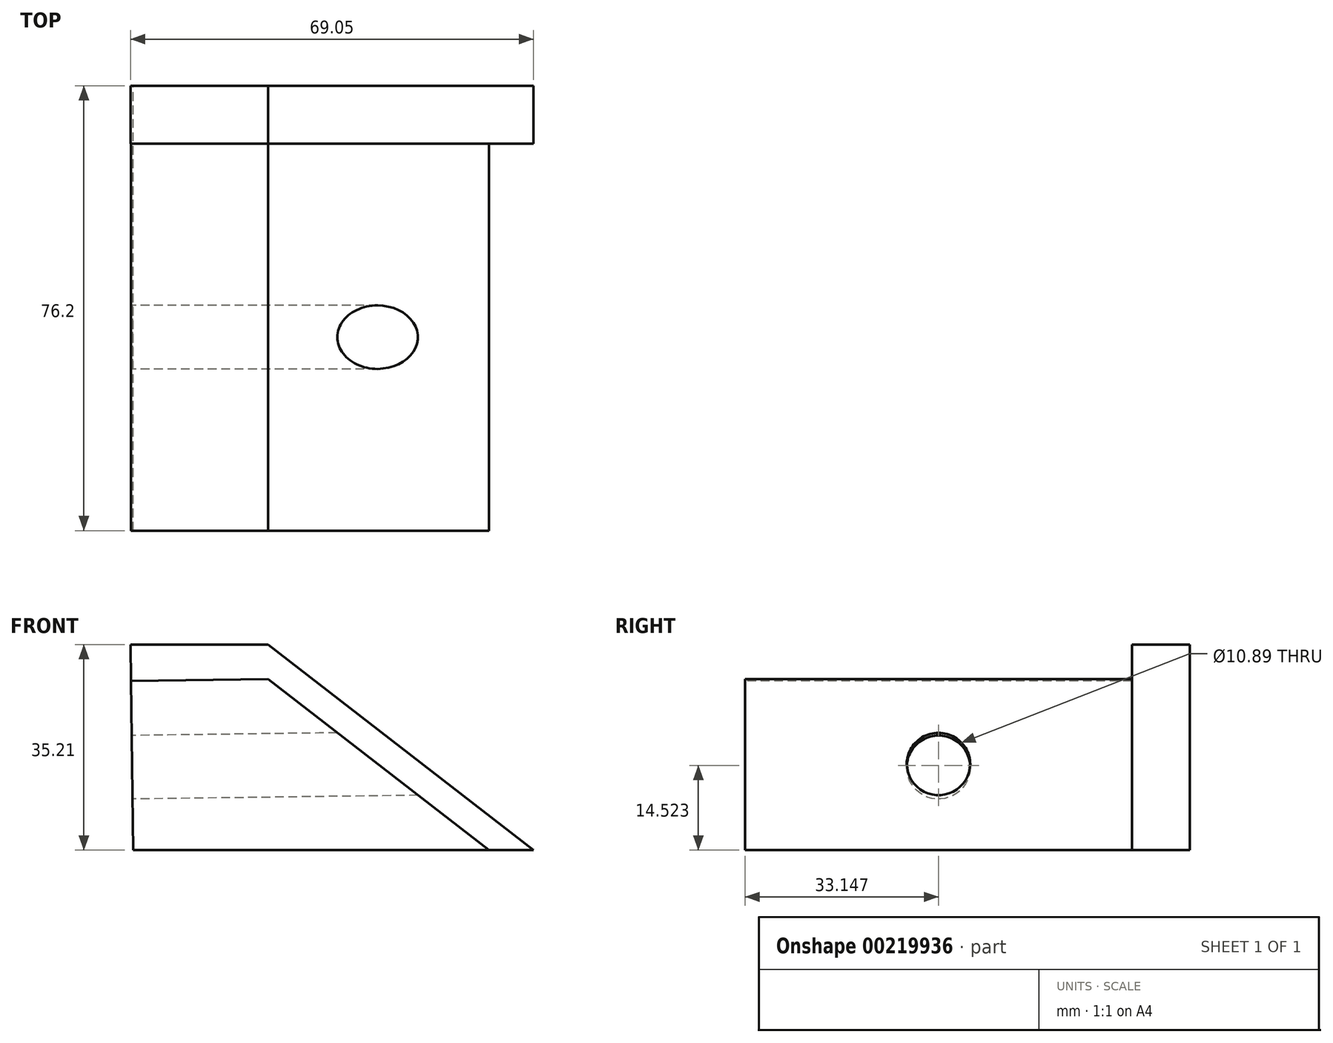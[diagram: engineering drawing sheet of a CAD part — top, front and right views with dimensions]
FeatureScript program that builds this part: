
annotation { "Feature Type Name" : "Feature", "Feature Type Description" : "" }
export const myFeature = defineFeature(function(context is Context, id is Id, definition is map)
    precondition{}
    {
        {
            var Q0;
            Q0=qCreatedBy(makeId("Front.planeOp"),FACE);
            var sketch = newSketch(context, id + "F0", { "sketchPlane" : qUnion([Q0])});
            skLineSegment(sketch, "E0", {"start": v(-34.17, 0) * mm, "end": v(34.4, 0) * mm});
            skLineSegment(sketch, "E1", {"start": v(34.4, 0) * mm, "end": v(-11.08, 35.21) * mm});
            skLineSegment(sketch, "E2", {"start": v(-11.08, 35.21) * mm, "end": v(-34.64, 35.21) * mm});
            skLineSegment(sketch, "E3", {"start": v(-34.64, 35.21) * mm, "end": v(-34.17, 0) * mm});
            skSolve(sketch);
        }
        {
            var Q0;
            Q0 = qSketchRegion(id + "F0", true);
            extrude(context, id + "F1", {"entities" : qUnion([Q0]), "depth" : 76.2 * mm});
        }
        {
            var Q0;
            Q0=makeQuery(id+"F1.opExtrude","CAP_FACE",FACE,{"disambiguationData":[OSD([sQuery(id+"F0.wireOp",EDGE,"E0"),sQuery(id+"F0.wireOp",EDGE,"E1"),sQuery(id+"F0.wireOp",EDGE,"E2"),sQuery(id+"F0.wireOp",EDGE,"E3")])],"isStart":false});
            var sketch = newSketch(context, id + "F2", { "sketchPlane" : qUnion([Q0])});
            skLineSegment(sketch, "E4", {"start": v(26.75, 0) * mm, "end": v(34.4, 0) * mm});
            skLineSegment(sketch, "E5", {"start": v(34.4, 0) * mm, "end": v(-11.08, 35.21) * mm});
            skLineSegment(sketch, "E6", {"start": v(-11.08, 35.21) * mm, "end": v(-34.64, 35.21) * mm});
            skLineSegment(sketch, "E7", {"start": v(-34.64, 35.21) * mm, "end": v(-34.55, 28.98) * mm});
            skLineSegment(sketch, "E8", {"start": v(-34.55, 28.98) * mm, "end": v(-11.08, 29.3) * mm});
            skLineSegment(sketch, "E9", {"start": v(-11.08, 29.3) * mm, "end": v(26.75, 0) * mm});
            skSolve(sketch);
        }
        {
            var Q0;
            Q0 = qSketchRegion(id + "F2", true);
            extrude(context, id + "F3", {"entities" : qUnion([Q0]), "operationType" : NewBodyOperationType.REMOVE, "oppositeDirection" : true, "depth" : 66.3 * mm});
        }
        {
            var Q0;
            Q0=makeQuery(id+"F1.opExtrude","SWEPT_FACE",FACE,{"disambiguationData":[OSD([sQuery(id+"F0.wireOp",EDGE,"E3")])]});
            var sketch = newSketch(context, id + "F4", { "sketchPlane" : qUnion([Q0])});
            skLineSegment(sketch, "E10.bottom", {"start": v(9.9, 29.43) * mm, "end": v(76.2, 29.43) * mm});
            skLineSegment(sketch, "E10.top", {"start": v(9.9, 0.45) * mm, "end": v(76.2, 0.45) * mm});
            skLineSegment(sketch, "E10.left", {"start": v(9.9, 29.43) * mm, "end": v(9.9, 0.45) * mm});
            skLineSegment(sketch, "E10.right", {"start": v(76.2, 29.43) * mm, "end": v(76.2, 0.45) * mm});
            skCircle(sketch, "E11", {"center": v(43.05, 14.65) * mm, "radius": 5.44 * mm});
            skPoint(sketch, "E11.centerSnap0", {"position": v(43.05, 0.45) * mm});
            skSolve(sketch);
        }
        {
            var Q0;
            Q0=makeQuery(id+"F4.imprint","IMPRINT",FACE,{"disambiguationData":[TD([[makeQuery(id+"F4.imprint","IMPRINT",EDGE,{"derivedFrom":sQuery(id+"F4.wireOp",EDGE,"E11")}),1.0]])]});
            extrude(context, id + "F5", {"entities" : qUnion([Q0]), "operationType" : NewBodyOperationType.REMOVE, "oppositeDirection" : true, "depth" : 87.88 * mm});
        }
    });
